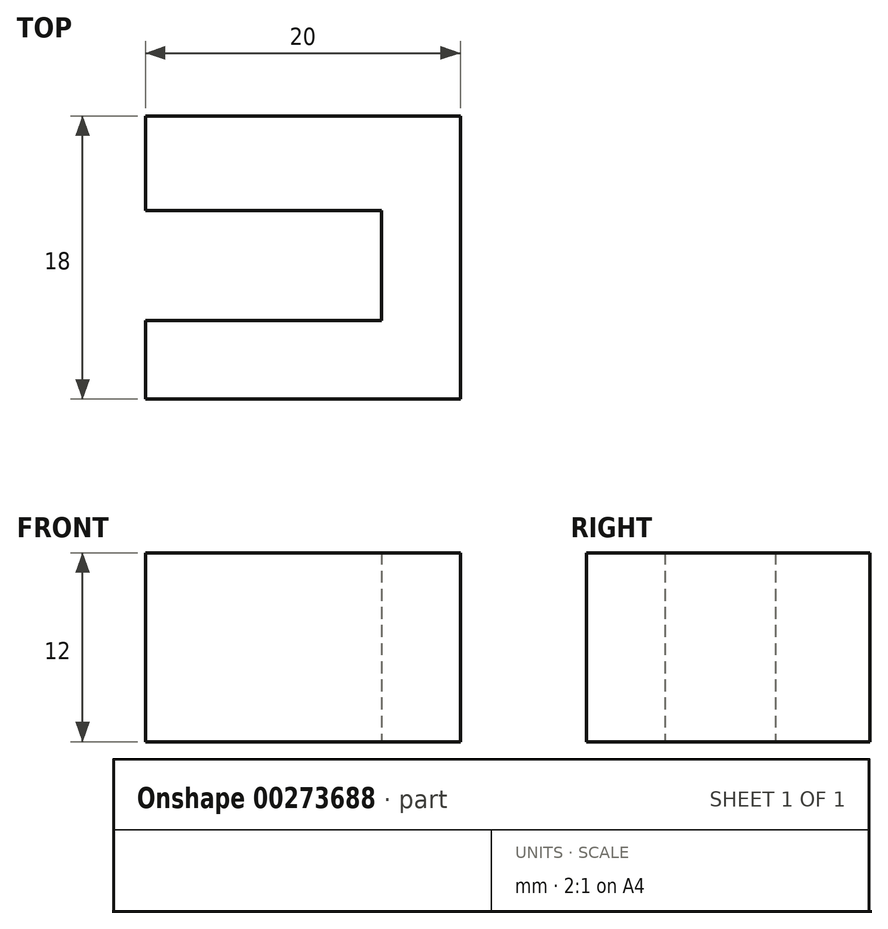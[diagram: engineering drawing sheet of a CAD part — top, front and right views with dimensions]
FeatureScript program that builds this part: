
annotation { "Feature Type Name" : "Feature", "Feature Type Description" : "" }
export const myFeature = defineFeature(function(context is Context, id is Id, definition is map)
    precondition{}
    {
        {
            var Q0;
            Q0=qCreatedBy(makeId("Top.planeOp"),FACE);
            var sketch = newSketch(context, id + "F0", { "sketchPlane" : qUnion([Q0])});
            skLineSegment(sketch, "E0.bottom", {"start": v(-20, 18) * mm, "end": v(0, 18) * mm});
            skLineSegment(sketch, "E0.top", {"start": v(-20, 12) * mm, "end": v(0, 12) * mm});
            skLineSegment(sketch, "E0.left", {"start": v(-20, 18) * mm, "end": v(-20, 12) * mm});
            skLineSegment(sketch, "E0.right", {"start": v(0, 18) * mm, "end": v(0, 12) * mm});
            skLineSegment(sketch, "E1.bottom", {"start": v(0, 18) * mm, "end": v(-5, 18) * mm});
            skLineSegment(sketch, "E1.top", {"start": v(0, 0) * mm, "end": v(-5, 0) * mm});
            skLineSegment(sketch, "E1.left", {"start": v(0, 18) * mm, "end": v(0, 0) * mm});
            skLineSegment(sketch, "E1.right", {"start": v(-5, 18) * mm, "end": v(-5, 0) * mm});
            skLineSegment(sketch, "E2.bottom", {"start": v(-5, 0) * mm, "end": v(-20, 0) * mm});
            skLineSegment(sketch, "E2.top", {"start": v(-5, 5) * mm, "end": v(-20, 5) * mm});
            skLineSegment(sketch, "E2.left", {"start": v(-5, 0) * mm, "end": v(-5, 5) * mm});
            skLineSegment(sketch, "E2.right", {"start": v(-20, 0) * mm, "end": v(-20, 5) * mm});
            skSolve(sketch);
        }
        {
            var Q0;
            Q0 = qSketchRegion(id + "F0", true);
            extrude(context, id + "F1", {"entities" : qUnion([Q0]), "depth" : 12 * mm});
        }
    });
